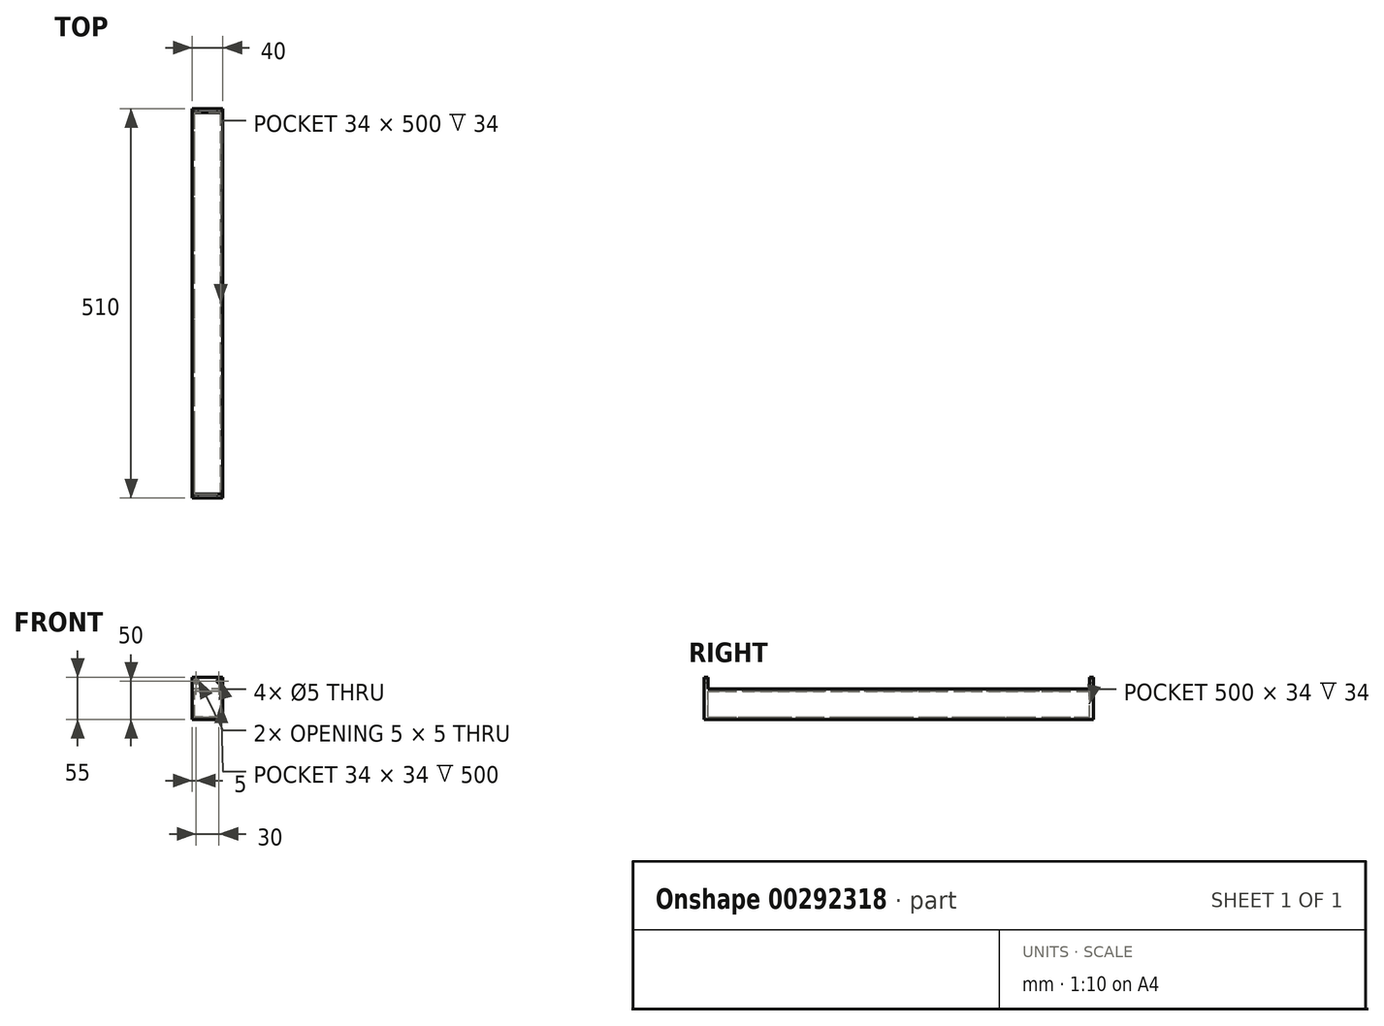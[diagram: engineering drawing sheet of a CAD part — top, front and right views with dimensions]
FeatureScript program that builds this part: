
annotation { "Feature Type Name" : "Feature", "Feature Type Description" : "" }
export const myFeature = defineFeature(function(context is Context, id is Id, definition is map)
    precondition{}
    {
        {
            var Q0;
            Q0=qCreatedBy(makeId("Front.planeOp"),FACE);
            var sketch = newSketch(context, id + "F0", { "sketchPlane" : qUnion([Q0])});
            skLineSegment(sketch, "E0.bottom", {"start": v(17, -17) * mm, "end": v(-17, -17) * mm});
            skLineSegment(sketch, "E0.top", {"start": v(17, 17) * mm, "end": v(-17, 17) * mm});
            skLineSegment(sketch, "E0.left", {"start": v(17, -17) * mm, "end": v(17, 17) * mm});
            skLineSegment(sketch, "E0.right", {"start": v(-17, -17) * mm, "end": v(-17, 17) * mm});
            skPoint(sketch, "E0.middle", {"position": v(0, 0) * mm});
            skLineSegment(sketch, "E1.bottom", {"start": v(20, -20) * mm, "end": v(-20, -20) * mm});
            skLineSegment(sketch, "E1.top", {"start": v(20, 20) * mm, "end": v(-20, 20) * mm});
            skLineSegment(sketch, "E1.left", {"start": v(20, -20) * mm, "end": v(20, 20) * mm});
            skLineSegment(sketch, "E1.right", {"start": v(-20, -20) * mm, "end": v(-20, 20) * mm});
            skSolve(sketch);
        }
        {
            var Q0;
            Q0 = qSketchRegion(id + "F0", true);
            extrude(context, id + "F1", {"entities" : qUnion([Q0]), "endBound" : BoundingType.SYMMETRIC, "depth" : 500 * mm});
        }
        {
            var Q0;
            Q0=qCreatedBy(makeId("Right.planeOp"),FACE);
            var sketch = newSketch(context, id + "F2", { "sketchPlane" : qUnion([Q0])});
            skLineSegment(sketch, "E2.bottom", {"start": v(-250, 35) * mm, "end": v(-255, 35) * mm});
            skLineSegment(sketch, "E2.top", {"start": v(-250, -20) * mm, "end": v(-255, -20) * mm});
            skLineSegment(sketch, "E2.left", {"start": v(-250, 35) * mm, "end": v(-250, -20) * mm});
            skLineSegment(sketch, "E2.right", {"start": v(-255, 35) * mm, "end": v(-255, -20) * mm});
            skLineSegment(sketch, "E3.MirrorCS", {"start": v(250, -20) * mm, "end": v(255, -20) * mm});
            skLineSegment(sketch, "E4.MirrorCS", {"start": v(250, 35) * mm, "end": v(255, 35) * mm});
            skLineSegment(sketch, "E5.MirrorCS", {"start": v(250, 35) * mm, "end": v(250, -20) * mm});
            skLineSegment(sketch, "E6.MirrorCS", {"start": v(255, 35) * mm, "end": v(255, -20) * mm});
            skSolve(sketch);
        }
        {
            var Q0;
            Q0 = qSketchRegion(id + "F2", true);
            extrude(context, id + "F3", {"entities" : qUnion([Q0]), "operationType" : NewBodyOperationType.ADD, "endBound" : BoundingType.SYMMETRIC, "depth" : 40 * mm});
        }
        {
            var Q0;
            Q0=qCreatedBy(makeId("Front.planeOp"),FACE);
            var sketch = newSketch(context, id + "F4", { "sketchPlane" : qUnion([Q0])});
            skCircle(sketch, "E7", {"center": v(-15, 30) * mm, "radius": 2.5 * mm});
            skCircle(sketch, "E8", {"center": v(15, 30) * mm, "radius": 2.5 * mm});
            skSolve(sketch);
        }
        {
            var Q0;
            Q0 = qSketchRegion(id + "F4", true);
            extrude(context, id + "F5", {"entities" : qUnion([Q0]), "operationType" : NewBodyOperationType.REMOVE, "endBound" : BoundingType.SYMMETRIC, "oppositeDirection" : true, "depth" : 510 * mm});
        }
    });
